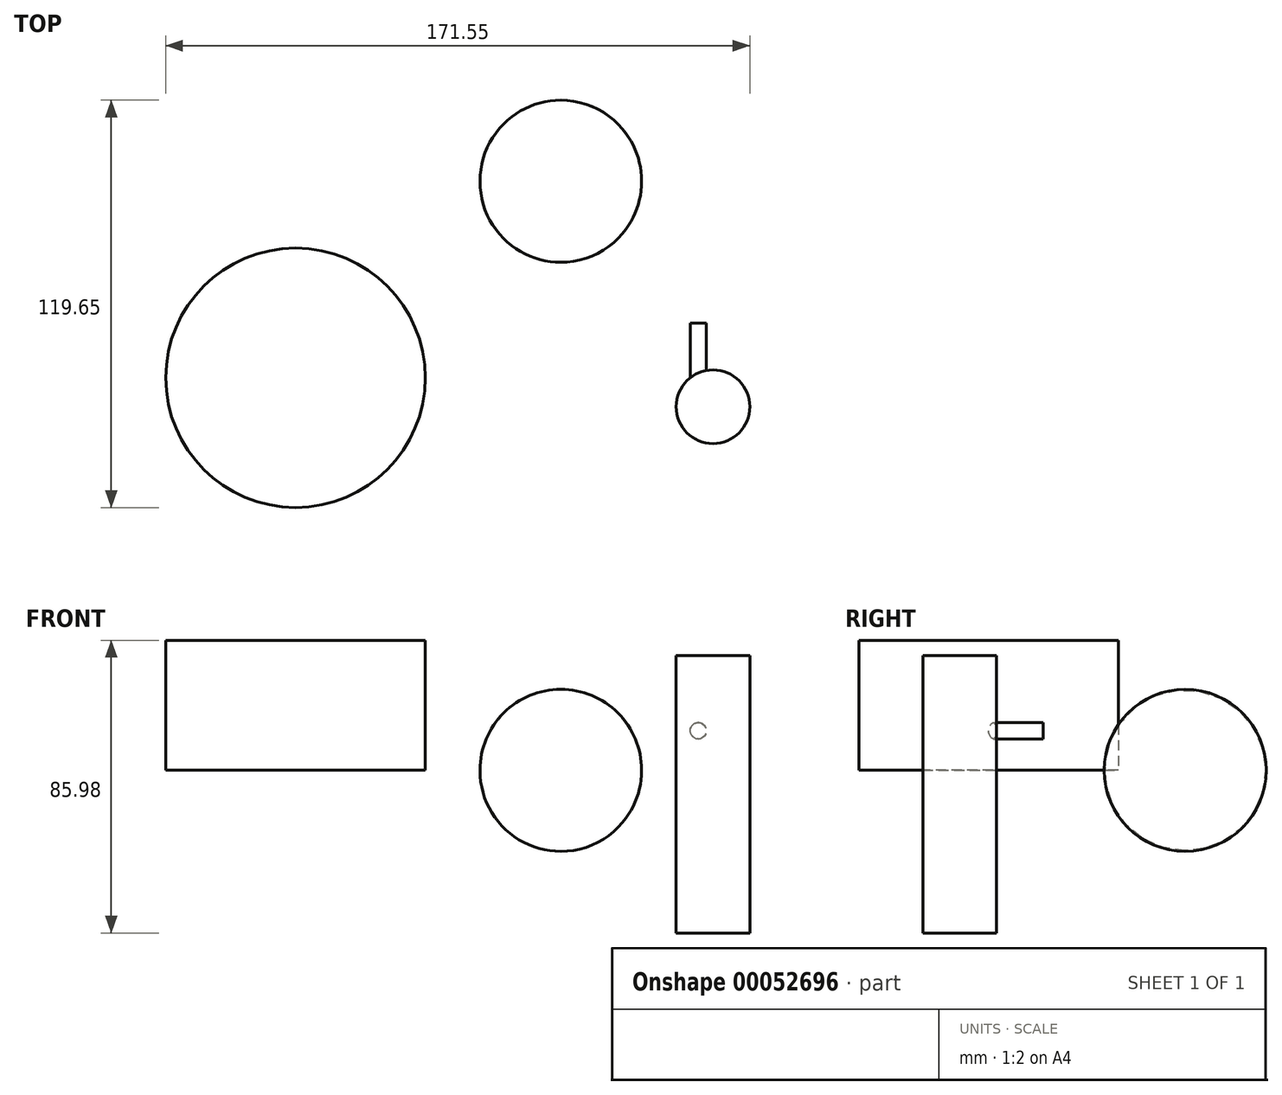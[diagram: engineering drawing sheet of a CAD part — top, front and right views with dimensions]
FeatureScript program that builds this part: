
annotation { "Feature Type Name" : "Feature", "Feature Type Description" : "" }
export const myFeature = defineFeature(function(context is Context, id is Id, definition is map)
    precondition{}
    {
        {
            var Q0;
            Q0=qCreatedBy(makeId("Top.planeOp"),FACE);
            var sketch = newSketch(context, id + "F0", { "sketchPlane" : qUnion([Q0])});
            skCircle(sketch, "E0", {"center": v(-43.49, -57.74) * mm, "radius": 38.1 * mm});
            skSolve(sketch);
        }
        {
            var Q0;
            Q0 = qSketchRegion(id + "F0", true);
            extrude(context, id + "F1", {"entities" : qUnion([Q0]), "depth" : 38.2 * mm});
        }
        {
            var Q0;
            Q0=qCreatedBy(makeId("Top.planeOp"),FACE);
            var sketch = newSketch(context, id + "F2", { "sketchPlane" : qUnion([Q0])});
            skCircle(sketch, "E1", {"center": v(79.13, -66.24) * mm, "radius": 10.83 * mm});
            skSolve(sketch);
        }
        {
            var Q0;
            Q0 = qSketchRegion(id + "F2", true);
            extrude(context, id + "F3", {"entities" : qUnion([Q0]), "depth" : 33.66 * mm});
        }
        {
            var Q0;
            Q0=qCreatedBy(makeId("Top.planeOp"),FACE);
            var sketch = newSketch(context, id + "F4", { "sketchPlane" : qUnion([Q0])});
            skArc(sketch, "E2", {"start": v(58.14, 0) * mm, "mid": v(34.42, 23.81) * mm, "end": v(10.7, 0) * mm});
            skLineSegment(sketch, "E3", {"start": v(10.7, 0) * mm, "end": v(58.14, 0) * mm});
            skSolve(sketch);
        }
        {
            var Q0;
            Q0 = qSketchRegion(id + "F4", true);
            var Q1;
            Q1=sQuery(id+"F4.wireOp",EDGE,"E3");
            revolve(context, id + "F5", {"entities" : qUnion([Q0]), "axis" : qUnion([Q1]), "revolveType" : RevolveType.FULL});
        }
        {
            var Q0;
            Q0=qCreatedBy(makeId("Front.planeOp"),FACE);
            var sketch = newSketch(context, id + "F6", { "sketchPlane" : qUnion([Q0])});
            skCircle(sketch, "E4", {"center": v(0, -45.41) * mm, "radius": 2.37 * mm});
            skSolve(sketch);
        }
        {
            var Q0;
            Q0 = qSketchRegion(id + "F6", true);
            extrude(context, id + "F7", {"entities" : qUnion([Q0]), "depth" : 25.4 * mm});
        }
        {
            var Q0;
            Q0=makeQuery(id+"F7.opExtrude","SWEPT_BODY",BODY,{"disambiguationData":[OSD([sQuery(id+"F6.wireOp",EDGE,"E4")])]});
            transform(context, id + "F8", {"entities" : qUnion([Q0]), "transformType" : TransformType.TRANSLATION_3D, "dx" : 74.81 * mm, "dy" : -41.69 * mm, "dz" : 57.03 * mm, "makeCopy" : false});
        }
        {
            var Q0;
            Q0=makeQuery(id+"F3.opExtrude","CAP_FACE",FACE,{"disambiguationData":[OSD([sQuery(id+"F2.wireOp",EDGE,"E1")])],"isStart":false});
            extrude(context, id + "F9", {"entities" : qUnion([Q0]), "operationType" : NewBodyOperationType.ADD, "oppositeDirection" : true, "depth" : 81.44 * mm});
        }
    });
